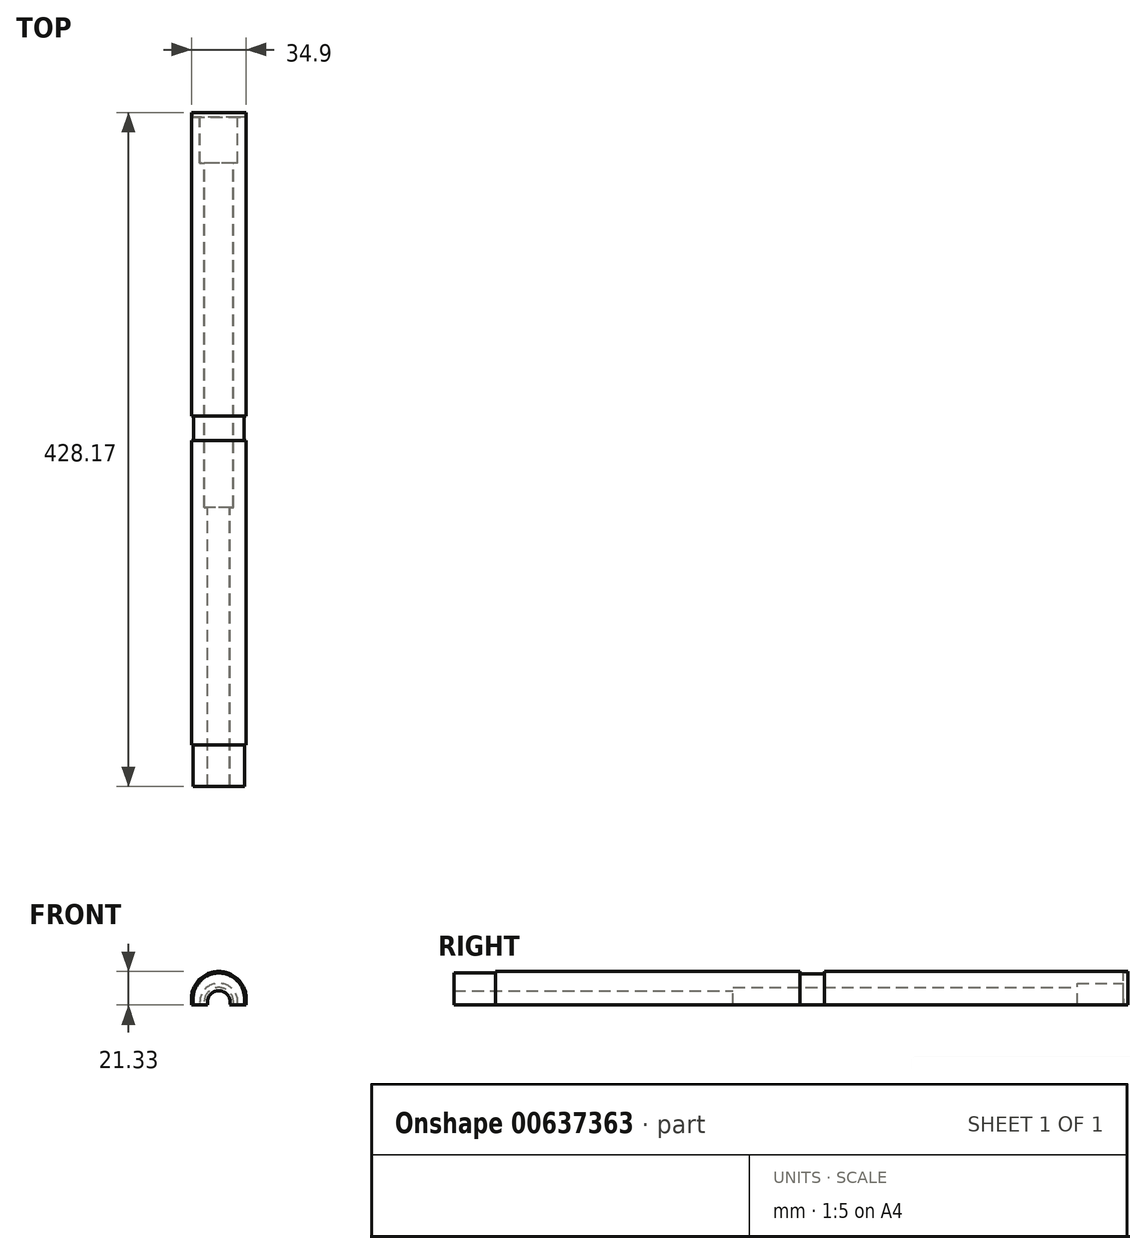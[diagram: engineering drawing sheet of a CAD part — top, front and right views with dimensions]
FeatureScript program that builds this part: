
annotation { "Feature Type Name" : "Feature", "Feature Type Description" : "" }
export const myFeature = defineFeature(function(context is Context, id is Id, definition is map)
    precondition{}
    {
        {
            var Q0;
            Q0=qCreatedBy(makeId("Front.planeOp"),FACE);
            var sketch = newSketch(context, id + "F0", { "sketchPlane" : qUnion([Q0])});
            skLineSegment(sketch, "E0", {"start": v(17.45, -4.64) * mm, "end": v(11.93, -4.64) * mm});
            skLineSegment(sketch, "E1.trimOffspring", {"start": v(-11.93, -4.64) * mm, "end": v(-17.45, -4.64) * mm});
            skLineSegment(sketch, "E2.MirrorCS", {"start": v(17.45, -4.64) * mm, "end": v(17.45, -0.86) * mm});
            skArc(sketch, "E3", {"start": v(17.45, -0.86) * mm, "mid": v(0, 16.7) * mm, "end": v(-17.45, -0.86) * mm});
            skLineSegment(sketch, "E4", {"start": v(-17.45, -0.86) * mm, "end": v(-17.45, -4.64) * mm});
            skArc(sketch, "E5", {"start": v(11.93, -4.64) * mm, "mid": v(0, 9.2) * mm, "end": v(-11.93, -4.64) * mm});
            skSolve(sketch);
        }
        {
            var Q0;
            Q0=makeQuery(id+"F0.imprint","IMPRINT",FACE,{"disambiguationData":[TD([[makeQuery(id+"F0.imprint","IMPRINT",EDGE,{"derivedFrom":sQuery(id+"F0.wireOp",EDGE,"E0")}),-1.0]])]});
            extrude(context, id + "F1", {"entities" : qUnion([Q0]), "depth" : 29.2 * mm, "offsetDistance" : 25.4 * mm});
        }
        {
            var Q0;
            Q0=makeQuery(id+"F1.opExtrude","CAP_FACE",FACE,{"disambiguationData":[OSD([sQuery(id+"F0.wireOp",EDGE,"E0"),sQuery(id+"F0.wireOp",EDGE,"E1.trimOffspring"),sQuery(id+"F0.wireOp",EDGE,"E2.MirrorCS"),sQuery(id+"F0.wireOp",EDGE,"E3"),sQuery(id+"F0.wireOp",EDGE,"E4"),sQuery(id+"F0.wireOp",EDGE,"E5")])],"isStart":false});
            var sketch = newSketch(context, id + "F2", { "sketchPlane" : qUnion([Q0])});
            skArc(sketch, "E6", {"start": v(9.11, -4.64) * mm, "mid": v(0, 6.5) * mm, "end": v(-9.11, -4.64) * mm});
            skLineSegment(sketch, "E7", {"start": v(-17.45, -4.64) * mm, "end": v(-9.11, -4.64) * mm});
            skLineSegment(sketch, "E8", {"start": v(-17.45, -0.86) * mm, "end": v(-17.45, -4.64) * mm});
            skLineSegment(sketch, "E9", {"start": v(17.45, -0.86) * mm, "end": v(17.45, -4.64) * mm});
            skLineSegment(sketch, "E10", {"start": v(17.45, -4.64) * mm, "end": v(9.11, -4.64) * mm});
            skArc(sketch, "E11", {"start": v(17.45, -0.86) * mm, "mid": v(0, 16.7) * mm, "end": v(-17.45, -0.86) * mm});
            skSolve(sketch);
        }
        {
            var Q0;
            {var subQ0=sQuery(id+"F2.wireOp",EDGE,"E6");Q0=makeQuery(id+"F2.imprint","IMPRINT",FACE,{"disambiguationData":[TD([[makeQuery(id+"F2.imprint","IMPRINT",EDGE,{"derivedFrom":subQ0}),-1.0]])]});}
            var Q1;
            {var subQ1=sQuery(id+"F2.wireOp",EDGE,"E8");Q1=makeQuery(id+"F2.imprint","IMPRINT",FACE,{"disambiguationData":[TD([[makeQuery(id+"F2.imprint","IMPRINT",EDGE,{"derivedFrom":subQ1}),1.0]])]});}
            extrude(context, id + "F3", {"entities" : qUnion([Q0, Q1]), "operationType" : NewBodyOperationType.ADD, "depth" : 160.55 * mm, "offsetDistance" : 25.4 * mm});
        }
        {
            var Q0;
            Q0=makeQuery(id+"F3.opExtrude","CAP_FACE",FACE,{"disambiguationData":[OSD([sQuery(id+"F2.wireOp",EDGE,"E6"),sQuery(id+"F2.wireOp",EDGE,"E7"),sQuery(id+"F2.wireOp",EDGE,"E8"),sQuery(id+"F2.wireOp",EDGE,"E9"),sQuery(id+"F2.wireOp",EDGE,"E10"),sQuery(id+"F2.wireOp",EDGE,"E11")])],"isStart":false});
            var sketch = newSketch(context, id + "F4", { "sketchPlane" : qUnion([Q0])});
            skArc(sketch, "E12.0", {"start": v(15.93, -0.85) * mm, "mid": v(0, 15.17) * mm, "end": v(-15.93, -0.85) * mm});
            skLineSegment(sketch, "E13", {"start": v(15.93, -0.85) * mm, "end": v(15.93, -4.64) * mm});
            skLineSegment(sketch, "E14", {"start": v(-15.93, -0.85) * mm, "end": v(-15.9, -4.64) * mm});
            skLineSegment(sketch, "E15", {"start": v(9.11, -4.64) * mm, "end": v(15.93, -4.64) * mm});
            skLineSegment(sketch, "E16", {"start": v(-9.11, -4.64) * mm, "end": v(-15.9, -4.64) * mm});
            skSolve(sketch);
        }
        {
            var Q0;
            Q0=makeQuery(id+"F4.imprint","IMPRINT",FACE,{"disambiguationData":[TD([[makeQuery(id+"F4.imprint","IMPRINT",EDGE,{"derivedFrom":sQuery(id+"F4.wireOp",EDGE,"E12.0")}),1.0]])]});
            extrude(context, id + "F5", {"entities" : qUnion([Q0]), "operationType" : NewBodyOperationType.ADD, "depth" : 15.42 * mm, "offsetDistance" : 25.4 * mm});
        }
        {
            var Q0;
            Q0=makeQuery(id+"F5.opExtrude","CAP_FACE",FACE,{"disambiguationData":[OSD([sQuery(id+"F2.wireOp",EDGE,"E6"),sQuery(id+"F4.wireOp",EDGE,"E12.0"),sQuery(id+"F4.wireOp",EDGE,"E13"),sQuery(id+"F4.wireOp",EDGE,"E14"),sQuery(id+"F4.wireOp",EDGE,"E15"),sQuery(id+"F4.wireOp",EDGE,"E16")])],"isStart":false});
            var sketch = newSketch(context, id + "F6", { "sketchPlane" : qUnion([Q0])});
            skArc(sketch, "E17", {"start": v(9.11, -4.64) * mm, "mid": v(0, 6.5) * mm, "end": v(-9.11, -4.64) * mm});
            skLineSegment(sketch, "E18", {"start": v(-17.45, -4.64) * mm, "end": v(-9.11, -4.64) * mm});
            skLineSegment(sketch, "E19", {"start": v(-17.45, -0.86) * mm, "end": v(-17.45, -4.64) * mm});
            skLineSegment(sketch, "E20", {"start": v(17.45, -0.86) * mm, "end": v(17.45, -4.64) * mm});
            skLineSegment(sketch, "E21", {"start": v(17.45, -4.64) * mm, "end": v(9.11, -4.64) * mm});
            skArc(sketch, "E22", {"start": v(17.45, -0.86) * mm, "mid": v(0, 16.7) * mm, "end": v(-17.45, -0.86) * mm});
            skSolve(sketch);
        }
        {
            var Q0;
            {var subQ1=sQuery(id+"F6.wireOp",EDGE,"E17");Q0=makeQuery(id+"F6.imprint","IMPRINT",FACE,{"disambiguationData":[TD([[makeQuery(id+"F6.imprint","IMPRINT",EDGE,{"derivedFrom":subQ1}),-1.0]])]});}
            var Q1;
            {var subQ3=sQuery(id+"F6.wireOp",EDGE,"E19");Q1=makeQuery(id+"F6.imprint","IMPRINT",FACE,{"disambiguationData":[TD([[makeQuery(id+"F6.imprint","IMPRINT",EDGE,{"derivedFrom":subQ3}),1.0]])]});}
            extrude(context, id + "F7", {"entities" : qUnion([Q0, Q1]), "operationType" : NewBodyOperationType.ADD, "depth" : 42.52 * mm, "offsetDistance" : 25.4 * mm});
        }
        {
            var Q0;
            Q0=makeQuery(id+"F7.opExtrude","CAP_FACE",FACE,{"disambiguationData":[OSD([sQuery(id+"F6.wireOp",EDGE,"E17"),sQuery(id+"F6.wireOp",EDGE,"E18"),sQuery(id+"F6.wireOp",EDGE,"E19"),sQuery(id+"F6.wireOp",EDGE,"E20"),sQuery(id+"F6.wireOp",EDGE,"E21"),sQuery(id+"F6.wireOp",EDGE,"E22")])],"isStart":false});
            var sketch = newSketch(context, id + "F8", { "sketchPlane" : qUnion([Q0])});
            skLineSegment(sketch, "E23", {"start": v(-17.45, -0.86) * mm, "end": v(-17.45, -4.64) * mm});
            skLineSegment(sketch, "E24", {"start": v(17.45, -0.86) * mm, "end": v(17.45, -4.64) * mm});
            skArc(sketch, "E25", {"start": v(17.45, -0.86) * mm, "mid": v(0, 16.7) * mm, "end": v(-17.45, -0.86) * mm});
            skLineSegment(sketch, "E26", {"start": v(-17.45, -4.64) * mm, "end": v(-7, -4.64) * mm});
            skArc(sketch, "E27.converted", {"start": v(7, -4.64) * mm, "mid": v(0, 4.44) * mm, "end": v(-7, -4.64) * mm});
            skLineSegment(sketch, "E28.trimOffspring", {"start": v(7, -4.64) * mm, "end": v(17.45, -4.64) * mm});
            skSolve(sketch);
        }
        {
            var Q0;
            {var subQ2=sQuery(id+"F8.wireOp",EDGE,"E27.converted");Q0=makeQuery(id+"F8.imprint","IMPRINT",FACE,{"disambiguationData":[TD([[makeQuery(id+"F8.imprint","IMPRINT",EDGE,{"derivedFrom":subQ2}),-1.0]])]});}
            var Q1;
            {var subQ1=sQuery(id+"F8.wireOp",EDGE,"E23");Q1=makeQuery(id+"F8.imprint","IMPRINT",FACE,{"disambiguationData":[TD([[makeQuery(id+"F8.imprint","IMPRINT",EDGE,{"derivedFrom":subQ1}),1.0]])]});}
            extrude(context, id + "F9", {"entities" : qUnion([Q0, Q1]), "operationType" : NewBodyOperationType.ADD, "depth" : 177.32 * mm, "offsetDistance" : 25.4 * mm});
        }
        {
            var Q0;
            Q0=makeQuery(id+"F9.opExtrude","CAP_FACE",FACE,{"disambiguationData":[OSD([sQuery(id+"F8.wireOp",EDGE,"E23"),sQuery(id+"F8.wireOp",EDGE,"E24"),sQuery(id+"F8.wireOp",EDGE,"E25"),sQuery(id+"F8.wireOp",EDGE,"E26"),sQuery(id+"F8.wireOp",EDGE,"E27.converted"),sQuery(id+"F8.wireOp",EDGE,"E28.trimOffspring")])],"isStart":false});
            var sketch = newSketch(context, id + "F10", { "sketchPlane" : qUnion([Q0])});
            skArc(sketch, "E29.0", {"start": v(16.43, -0.86) * mm, "mid": v(0, 15.68) * mm, "end": v(-16.43, -0.86) * mm});
            skLineSegment(sketch, "E30.0", {"start": v(16.43, -4.64) * mm, "end": v(16.43, -0.86) * mm});
            skLineSegment(sketch, "E31.0", {"start": v(-16.43, -0.86) * mm, "end": v(-16.43, -4.64) * mm});
            skLineSegment(sketch, "E32", {"start": v(-17.45, -0.86) * mm, "end": v(-17.45, -4.64) * mm});
            skLineSegment(sketch, "E33", {"start": v(-16.43, -4.64) * mm, "end": v(-17.45, -4.64) * mm});
            skLineSegment(sketch, "E34", {"start": v(16.43, -4.64) * mm, "end": v(17.45, -4.64) * mm});
            skLineSegment(sketch, "E35", {"start": v(17.45, -4.64) * mm, "end": v(17.45, -0.86) * mm});
            skArc(sketch, "E36", {"start": v(17.45, -0.86) * mm, "mid": v(0, 16.7) * mm, "end": v(-17.45, -0.86) * mm});
            skLineSegment(sketch, "E37", {"start": v(-16.43, -4.64) * mm, "end": v(-7, -4.64) * mm});
            skLineSegment(sketch, "E38", {"start": v(16.43, -4.64) * mm, "end": v(7, -4.64) * mm});
            skLineSegment(sketch, "E39", {"start": v(0, 15.68) * mm, "end": v(0, 4.44) * mm});
            skArc(sketch, "E40", {"start": v(7, -4.64) * mm, "mid": v(0, 4.44) * mm, "end": v(-7, -4.64) * mm});
            skSolve(sketch);
        }
        {
            var Q0;
            Q0=makeQuery(id+"F10.imprint","IMPRINT",FACE,{"disambiguationData":[TD([[makeQuery(id+"F10.imprint","IMPRINT",EDGE,{"derivedFrom":sQuery(id+"F10.wireOp",EDGE,"E29.0")}),-1.0]])]});
            extrude(context, id + "F11", {"entities" : qUnion([Q0]), "operationType" : NewBodyOperationType.REMOVE, "oppositeDirection" : true, "depth" : 26.5 * mm, "offsetDistance" : 25.4 * mm});
        }
        {
            var Q0;
            Q0=makeQuery(id+"F1.opExtrude","CAP_FACE",FACE,{"disambiguationData":[OSD([sQuery(id+"F0.wireOp",EDGE,"E0"),sQuery(id+"F0.wireOp",EDGE,"E1.trimOffspring"),sQuery(id+"F0.wireOp",EDGE,"E2.MirrorCS"),sQuery(id+"F0.wireOp",EDGE,"E3"),sQuery(id+"F0.wireOp",EDGE,"E4"),sQuery(id+"F0.wireOp",EDGE,"E5")])],"isStart":true});
            var sketch = newSketch(context, id + "F12", { "sketchPlane" : qUnion([Q0])});
            skArc(sketch, "E41.0", {"start": v(-16.69, -0.86) * mm, "mid": v(0, 15.93) * mm, "end": v(16.69, -0.86) * mm});
            skLineSegment(sketch, "E42", {"start": v(16.69, -0.86) * mm, "end": v(16.67, -4.64) * mm});
            skLineSegment(sketch, "E43", {"start": v(-16.69, -0.86) * mm, "end": v(-16.69, -4.64) * mm});
            skLineSegment(sketch, "E44", {"start": v(16.67, -4.64) * mm, "end": v(11.93, -4.64) * mm});
            skLineSegment(sketch, "E45", {"start": v(-16.69, -4.64) * mm, "end": v(-11.93, -4.64) * mm});
            skArc(sketch, "E46", {"start": v(11.93, -4.64) * mm, "mid": v(0, 9.2) * mm, "end": v(-11.93, -4.64) * mm});
            skSolve(sketch);
        }
        {
            var Q0;
            Q0=makeQuery(id+"F12.imprint","IMPRINT",FACE,{"disambiguationData":[TD([[makeQuery(id+"F12.imprint","IMPRINT",EDGE,{"derivedFrom":sQuery(id+"F12.wireOp",EDGE,"E41.0")}),-1.0]])]});
            extrude(context, id + "F13", {"entities" : qUnion([Q0]), "operationType" : NewBodyOperationType.ADD, "depth" : 3.15 * mm, "offsetDistance" : 25.4 * mm});
        }
    });
